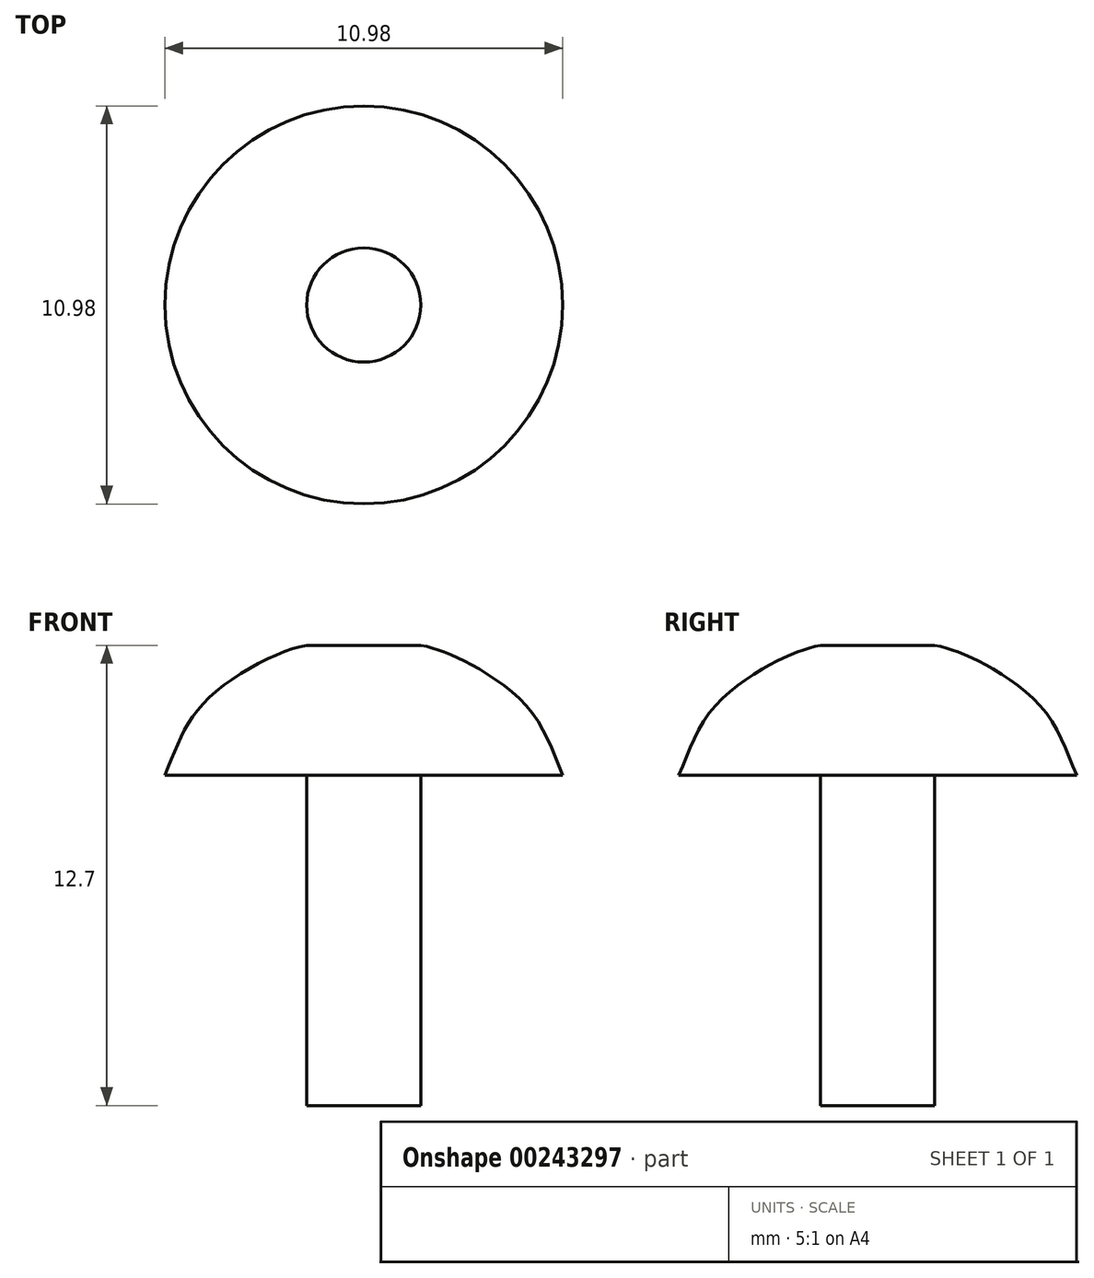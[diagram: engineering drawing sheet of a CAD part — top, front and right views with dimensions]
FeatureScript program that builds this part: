
annotation { "Feature Type Name" : "Feature", "Feature Type Description" : "" }
export const myFeature = defineFeature(function(context is Context, id is Id, definition is map)
    precondition{}
    {
        {
            var Q0;
            Q0=qCreatedBy(makeId("Front.planeOp"),FACE);
            var sketch = newSketch(context, id + "F0", { "sketchPlane" : qUnion([Q0])});
            skLineSegment(sketch, "E0.bottom", {"start": v(0, 0) * mm, "end": v(1.57, 0) * mm});
            skLineSegment(sketch, "E0.top", {"start": v(0, 12.7) * mm, "end": v(1.57, 12.7) * mm});
            skLineSegment(sketch, "E0.left", {"start": v(0, 0) * mm, "end": v(0, 12.7) * mm});
            skLineSegment(sketch, "E0.right", {"start": v(1.57, 0) * mm, "end": v(1.57, 9.11) * mm});
            skLineSegment(sketch, "E1", {"start": v(1.57, 9.11) * mm, "end": v(5.49, 9.11) * mm});
            skFitSpline(sketch, "E2", {"points": [v(5.49, 9.11) * mm, v(4.3, 11.22) * mm, v(1.57, 12.7) * mm], "startDerivative": vector(-2.19, 5.29) * mm, "endDerivative": vector(-4, 0.64) * mm});
            skSolve(sketch);
        }
        {
            var Q0;
            Q0=makeQuery(id+"F0.imprint","IMPRINT",FACE,{"disambiguationData":[TD([[makeQuery(id+"F0.imprint","IMPRINT",EDGE,{"derivedFrom":sQuery(id+"F0.wireOp",EDGE,"E0.bottom")}),1.0]])]});
            var Q1;
            Q1=sQuery(id+"F0.wireOp",EDGE,"E0.left");
            revolve(context, id + "F1", {"entities" : qUnion([Q0]), "axis" : qUnion([Q1]), "revolveType" : RevolveType.FULL});
        }
    });
